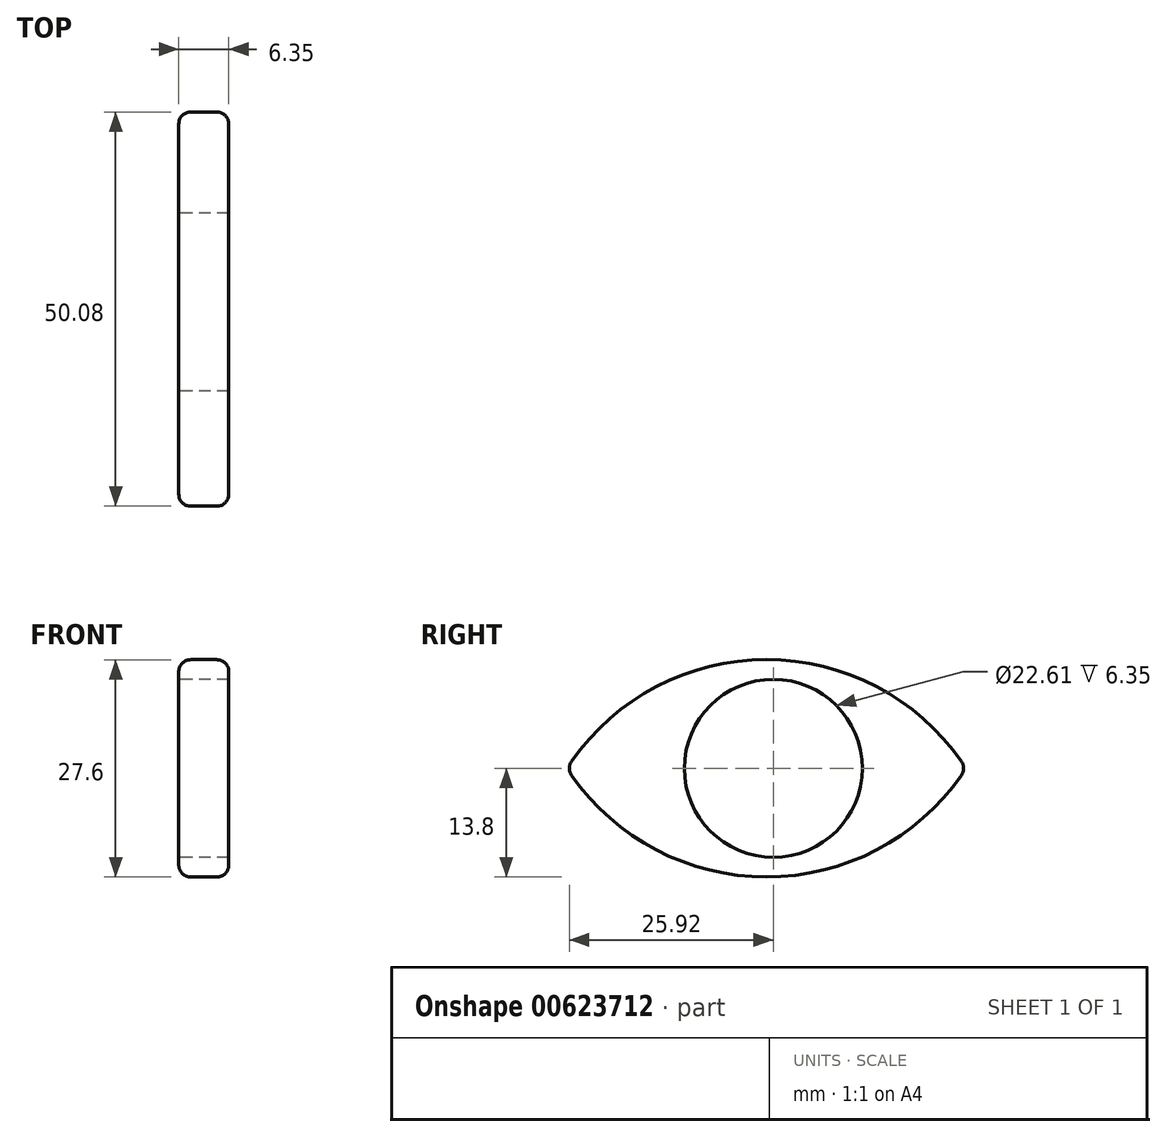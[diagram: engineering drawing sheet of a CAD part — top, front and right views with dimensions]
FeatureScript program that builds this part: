
annotation { "Feature Type Name" : "Feature", "Feature Type Description" : "" }
export const myFeature = defineFeature(function(context is Context, id is Id, definition is map)
    precondition{}
    {
        {
            var Q0;
            Q0=qCreatedBy(makeId("Right.planeOp"),FACE);
            var sketch = newSketch(context, id + "F0", { "sketchPlane" : qUnion([Q0])});
            skCircle(sketch, "E0", {"center": v(0, 0) * mm, "radius": 11.3 * mm});
            skArc(sketch, "E1", {"start": v(24.47, 0) * mm, "mid": v(-0.88, 13.8) * mm, "end": v(-26.23, 0) * mm});
            skArc(sketch, "E2.MirrorCS", {"start": v(24.47, 0) * mm, "mid": v(-0.88, -13.8) * mm, "end": v(-26.23, 0) * mm});
            skSolve(sketch);
        }
        {
            var Q0;
            Q0=makeQuery(id+"F0.imprint","IMPRINT",FACE,{"disambiguationData":[TD([[makeQuery(id+"F0.imprint","IMPRINT",EDGE,{"derivedFrom":sQuery(id+"F0.wireOp",EDGE,"E0")}),-1.0]])]});
            extrude(context, id + "F1", {"entities" : qUnion([Q0]), "depth" : 6.35 * mm, "offsetDistance" : 25.4 * mm});
        }
        {
            var Q0;
            Q0=makeQuery(id+"F1.opExtrude","CAP_EDGE",EDGE,{"disambiguationData":[OSD([sQuery(id+"F0.wireOp",EDGE,"E2.MirrorCS")])],"isStart":true});
            var Q1;
            Q1=makeQuery(id+"F1.opExtrude","CAP_EDGE",EDGE,{"disambiguationData":[OSD([sQuery(id+"F0.wireOp",EDGE,"E1")])],"isStart":true});
            var Q2;
            Q2=makeQuery(id+"F1.opExtrude","CAP_EDGE",EDGE,{"disambiguationData":[OSD([sQuery(id+"F0.wireOp",EDGE,"E2.MirrorCS")])],"isStart":false});
            var Q3;
            Q3=makeQuery(id+"F1.opExtrude","CAP_EDGE",EDGE,{"disambiguationData":[OSD([sQuery(id+"F0.wireOp",EDGE,"E1")])],"isStart":false});
            var Q4;
            {var subQ0=sQuery(id+"F0.wireOp",EDGE,"E2.MirrorCS");var subQ1=sQuery(id+"F0.wireOp",EDGE,"E1");Q4=makeQuery(id+"F1.opExtrude","SWEPT_EDGE",EDGE,{"disambiguationData":[OSD([subQ1,subQ0]),TDD([makeQuery(id+"F0.imprint","INTERSECT",VERTEX,{"disambiguationData":[OD(0.0)],"derivedFrom":[subQ1,subQ0]})])]});}
            var Q5;
            {var subQ0=sQuery(id+"F0.wireOp",EDGE,"E2.MirrorCS");var subQ1=sQuery(id+"F0.wireOp",EDGE,"E1");Q5=makeQuery(id+"F1.opExtrude","SWEPT_EDGE",EDGE,{"disambiguationData":[OSD([subQ1,subQ0]),TDD([makeQuery(id+"F0.imprint","INTERSECT",VERTEX,{"disambiguationData":[OD(1.0)],"derivedFrom":[subQ1,subQ0]})])]});}
            fillet(context, id + "F2", {"entities" : qUnion([Q0, Q1, Q2, Q3, Q4, Q5]), "radius" : 1.52 * mm, "tangentPropagation" : true, "allowEdgeOverflow" : false});
        }
    });
